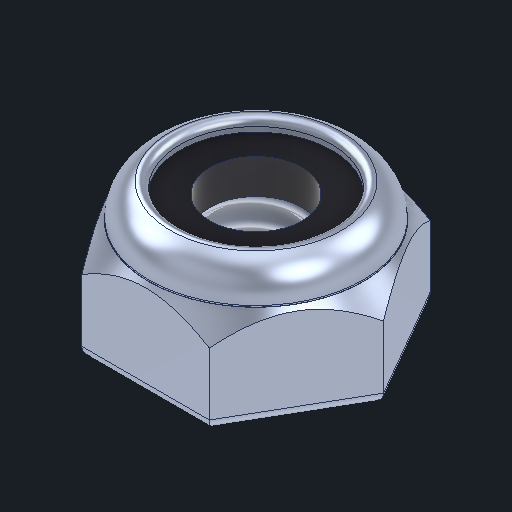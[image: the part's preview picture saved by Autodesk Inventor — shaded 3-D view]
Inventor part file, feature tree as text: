
AUTODESK INVENTOR PART (.ipt)
format: ipt  version: 2025 (Build 290162000, 162)  size: 229,376 bytes
history: native  units: in
note: dims shown in document units (in); Inventor stores cm internally (conversion verified against a paired STEP export)
features: other x4, sketch x2, plane x1
ambient origin geometry x8: Origin, YZ Plane, XZ Plane, XY Plane, X Axis, Y Axis, Z Axis, Center Point
bodies: Body1 (feature_tree)
feature tree (7):
  other  "Nut Thin Nylock.ipt"
  other  "NONE::Nut Thin Nylock.ipt"
  other  "TaggingFeature1"
  sketch  "Sketch1"  dims[d0=0.3937in]
  sketch  "Sketch2"
  plane  "Work Plane1"
  parser-record x1  (decoder bookkeeping rows leaked as tree rows — omitted from the tree; the rows remain in map.json)
